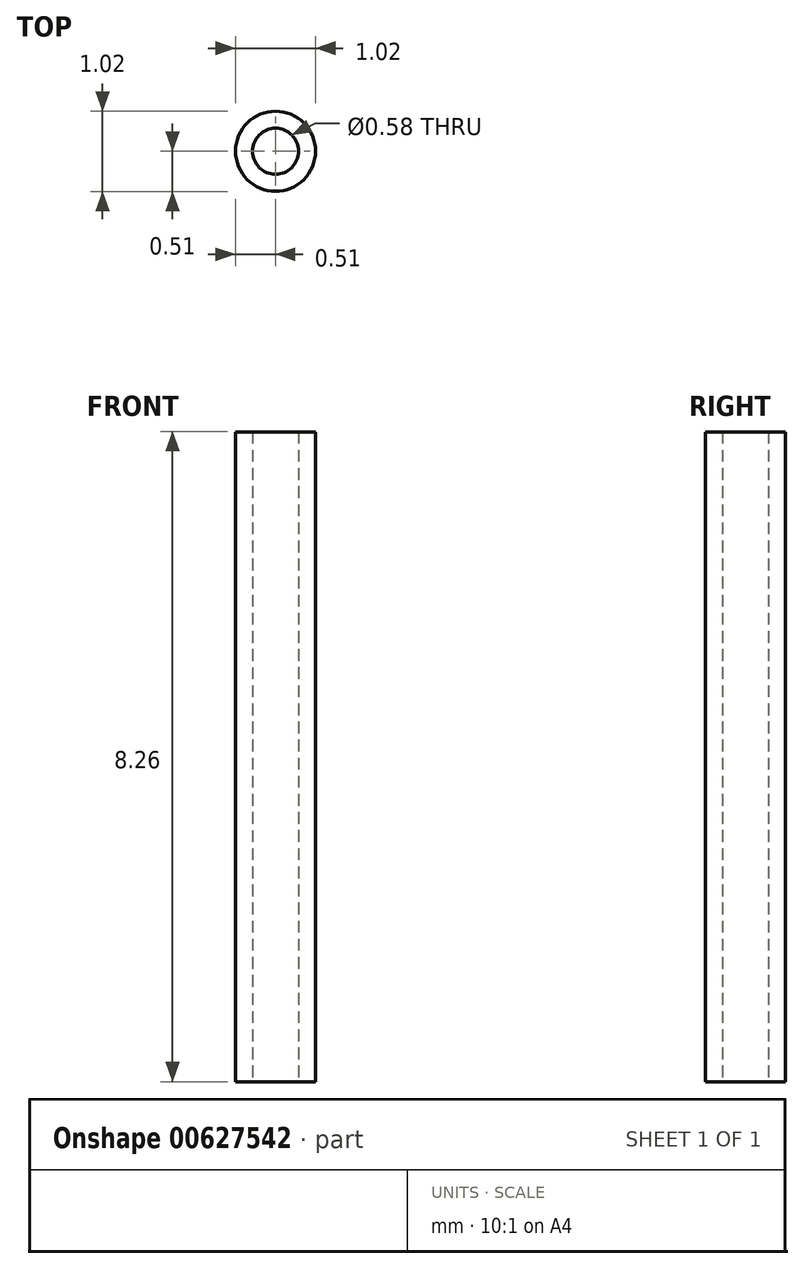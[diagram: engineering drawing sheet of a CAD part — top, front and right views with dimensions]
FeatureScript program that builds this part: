
annotation { "Feature Type Name" : "Feature", "Feature Type Description" : "" }
export const myFeature = defineFeature(function(context is Context, id is Id, definition is map)
    precondition{}
    {
        {
            var Q0;
            Q0=qCreatedBy(makeId("Front.planeOp"),FACE);
            var sketch = newSketch(context, id + "F0", { "sketchPlane" : qUnion([Q0])});
            skLineSegment(sketch, "E0", {"start": v(0, 0) * mm, "end": v(0, 8.22) * mm, "construction": true});
            skLineSegment(sketch, "E1.bottom", {"start": v(0.3, 0) * mm, "end": v(0.5, 0) * mm});
            skLineSegment(sketch, "E1.top", {"start": v(0.3, 8.26) * mm, "end": v(0.5, 8.26) * mm});
            skLineSegment(sketch, "E1.left", {"start": v(0.3, 0) * mm, "end": v(0.3, 8.26) * mm});
            skLineSegment(sketch, "E1.right", {"start": v(0.5, 0) * mm, "end": v(0.5, 8.26) * mm});
            skSolve(sketch);
        }
        {
            var Q0;
            Q0 = qSketchRegion(id + "F0", true);
            var Q1;
            Q1=sQuery(id+"F0.wireOp",EDGE,"E0");
            revolve(context, id + "F1", {"entities" : qUnion([Q0]), "axis" : qUnion([Q1]), "revolveType" : RevolveType.FULL});
        }
    });
